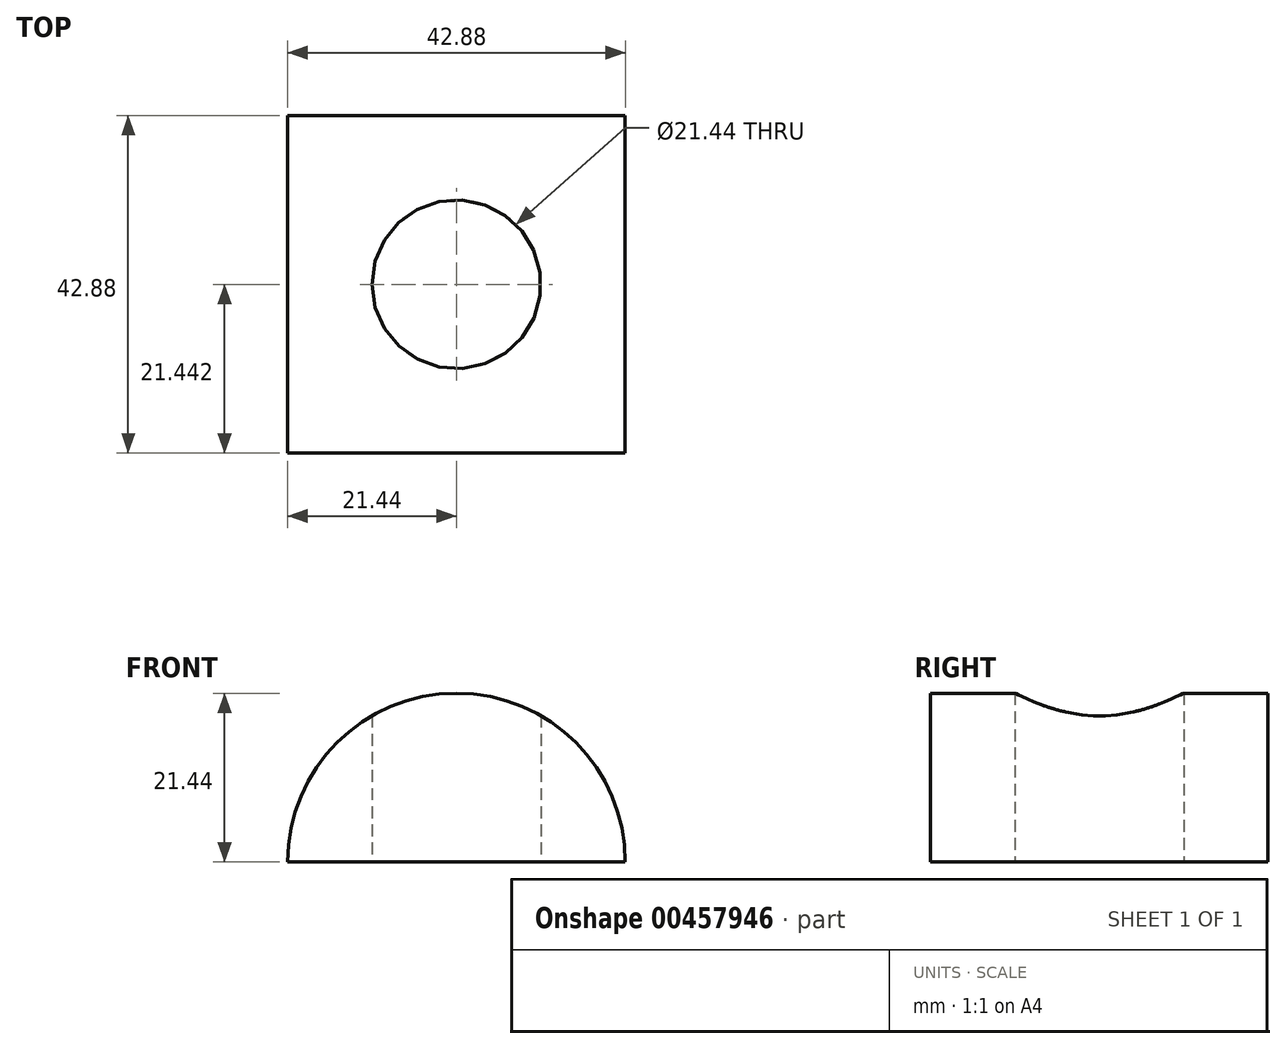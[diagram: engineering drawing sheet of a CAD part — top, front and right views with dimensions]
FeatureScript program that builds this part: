
annotation { "Feature Type Name" : "Feature", "Feature Type Description" : "" }
export const myFeature = defineFeature(function(context is Context, id is Id, definition is map)
    precondition{}
    {
        {
            var Q0;
            Q0=qCreatedBy(makeId("Front.planeOp"),FACE);
            var sketch = newSketch(context, id + "F0", { "sketchPlane" : qUnion([Q0])});
            skArc(sketch, "E0", {"start": v(21.44, 0) * mm, "mid": v(0, 21.44) * mm, "end": v(-21.44, 0) * mm});
            skLineSegment(sketch, "E1", {"start": v(-21.44, 0) * mm, "end": v(21.44, 0) * mm});
            skSolve(sketch);
        }
        {
            var Q0;
            Q0 = qSketchRegion(id + "F0", true);
            extrude(context, id + "F1", {"entities" : qUnion([Q0]), "depth" : 42.88 * mm});
        }
        {
            var Q0;
            Q0=makeQuery(id+"F1.opExtrude","SWEPT_FACE",FACE,{"disambiguationData":[OSD([sQuery(id+"F0.wireOp",EDGE,"E1")])]});
            var sketch = newSketch(context, id + "F2", { "sketchPlane" : qUnion([Q0])});
            skCircle(sketch, "E2", {"center": v(0, 21.44) * mm, "radius": 10.72 * mm});
            skSolve(sketch);
        }
        {
            var Q0;
            Q0 = qSketchRegion(id + "F2", true);
            extrude(context, id + "F3", {"entities" : qUnion([Q0]), "operationType" : NewBodyOperationType.REMOVE, "endBound" : BoundingType.THROUGH_ALL, "oppositeDirection" : true, "depth" : 25.4 * mm});
        }
    });
